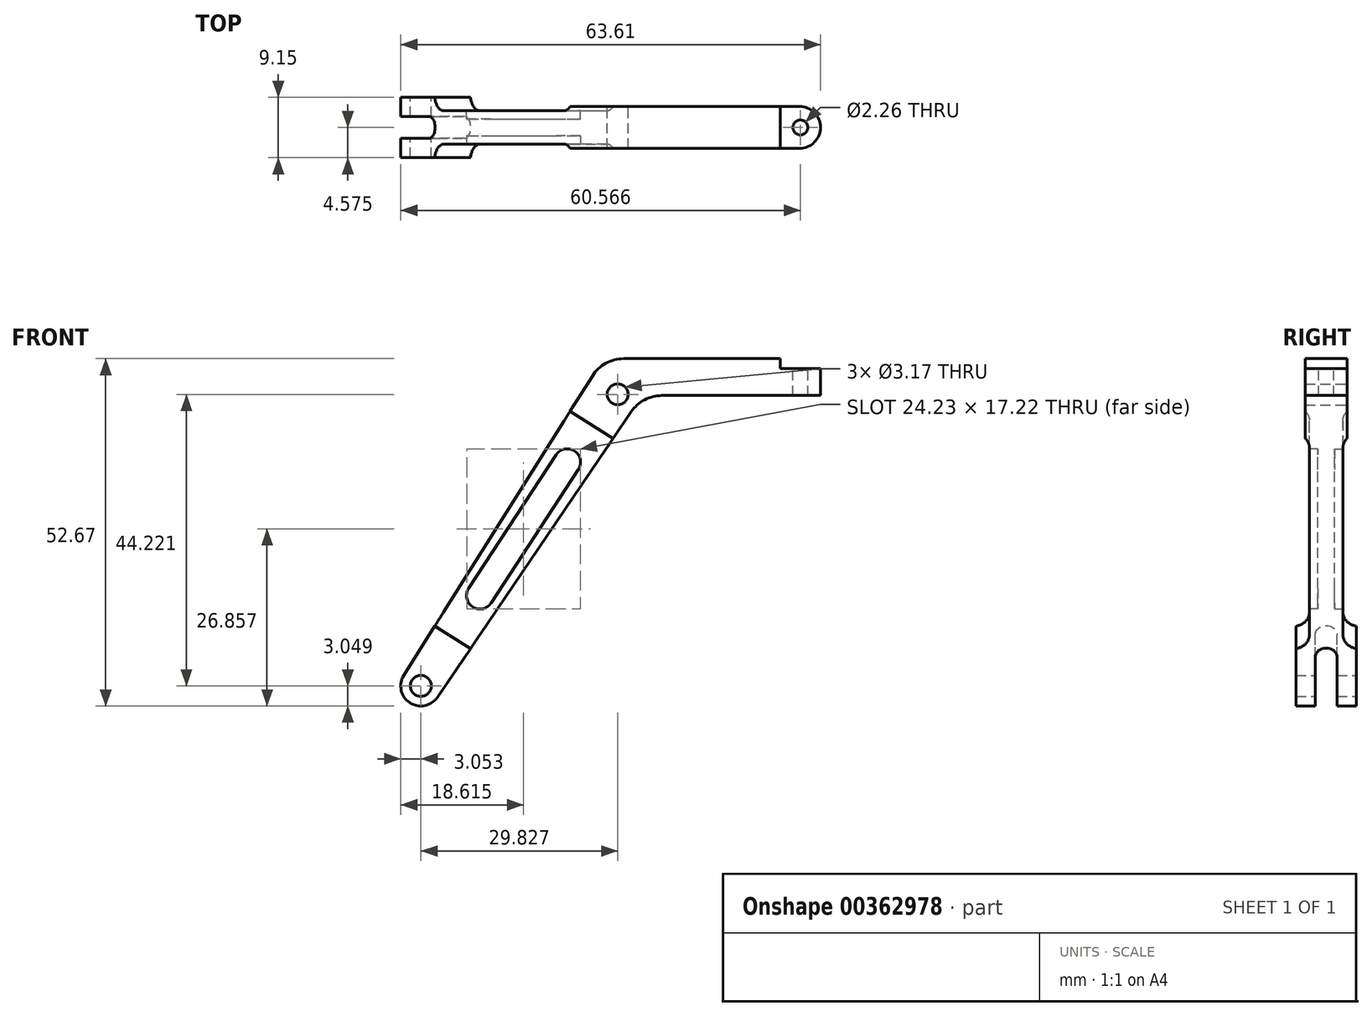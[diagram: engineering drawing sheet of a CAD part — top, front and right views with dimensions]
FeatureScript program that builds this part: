
annotation { "Feature Type Name" : "Feature", "Feature Type Description" : "" }
export const myFeature = defineFeature(function(context is Context, id is Id, definition is map)
    precondition{}
    {
        {
            var Q0;
            Q0=qCreatedBy(makeId("Front.planeOp"),FACE);
            var sketch = newSketch(context, id + "F0", { "sketchPlane" : qUnion([Q0])});
            skCircle(sketch, "E0", {"center": v(0, 0) * mm, "radius": 1.59 * mm});
            skLineSegment(sketch, "E1", {"start": v(30.73, -0.19) * mm, "end": v(30.73, 3.88) * mm});
            skLineSegment(sketch, "E2", {"start": v(0, 0) * mm, "end": v(-29.83, -44.22) * mm, "construction": true});
            skLineSegment(sketch, "E3", {"start": v(0, 0) * mm, "end": v(0, -37.53) * mm, "construction": true});
            skCircle(sketch, "E4", {"center": v(-29.83, -44.22) * mm, "radius": 1.59 * mm});
            skArc(sketch, "E5", {"start": v(-32.4, -42.6) * mm, "mid": v(-31.5, -46.77) * mm, "end": v(-27.3, -45.93) * mm});
            skLineSegment(sketch, "E6", {"start": v(-32.4, -42.6) * mm, "end": v(-3.83, 2.79) * mm});
            skLineSegment(sketch, "E7", {"start": v(0.9, 5.4) * mm, "end": v(24.64, 5.4) * mm});
            skPoint(sketch, "E8.visualSharp", {"position": v(-2.19, 5.4) * mm});
            skArc(sketch, "E8.filletArc", {"start": v(0.9, 5.4) * mm, "mid": v(-1.8, 4.7) * mm, "end": v(-3.83, 2.79) * mm});
            skLineSegment(sketch, "E9", {"start": v(-27.3, -45.93) * mm, "end": v(2.05, -2.64) * mm});
            skLineSegment(sketch, "E10.trimOffspring", {"start": v(6.68, -0.19) * mm, "end": v(30.73, -0.19) * mm});
            skPoint(sketch, "E11.visualSharp", {"position": v(3.72, -0.19) * mm});
            skArc(sketch, "E11.filletArc", {"start": v(6.68, -0.19) * mm, "mid": v(4.06, -0.84) * mm, "end": v(2.05, -2.64) * mm});
            skLineSegment(sketch, "E12", {"start": v(0, 9.08) * mm, "end": v(0, 14.2) * mm});
            skLineSegment(sketch, "E13", {"start": v(24.64, 5.4) * mm, "end": v(24.64, 3.88) * mm});
            skLineSegment(sketch, "E14", {"start": v(24.64, 3.88) * mm, "end": v(30.73, 3.88) * mm});
            skPoint(sketch, "E15.orphan", {"position": v(30.73, 5.4) * mm});
            skPoint(sketch, "E16.0.start.orphan", {"position": v(24.64, 9.08) * mm});
            skSolve(sketch);
        }
        {
            var Q0;
            Q0=makeQuery(id+"F0.imprint","IMPRINT",FACE,{"disambiguationData":[TD([[makeQuery(id+"F0.imprint","IMPRINT",EDGE,{"derivedFrom":sQuery(id+"F0.wireOp",EDGE,"E0")}),-1.0]])]});
            extrude(context, id + "F1", {"entities" : qUnion([Q0]), "depth" : 6.35 * mm});
        }
        {
            var Q0;
            Q0=makeQuery(id+"F1.opExtrude","SWEPT_FACE",FACE,{"disambiguationData":[OSD([sQuery(id+"F0.wireOp",EDGE,"E14")])]});
            var sketch = newSketch(context, id + "F2", { "sketchPlane" : qUnion([Q0])});
            skPoint(sketch, "E17", {"position": v(27.69, -3.18) * mm});
            skPoint(sketch, "E17.positionSnap0", {"position": v(30.73, -3.18) * mm});
            skSolve(sketch);
        }
        {
            var Q0;
            Q0=sQuery(id+"F2.wireOp",VERTEX,"E17");
            var Q1;
            Q1=makeQuery(id+"F1.opExtrude","SWEPT_BODY",BODY,{"disambiguationData":[OSD([sQuery(id+"F0.wireOp",EDGE,"E0"),sQuery(id+"F0.wireOp",EDGE,"E1"),sQuery(id+"F0.wireOp",EDGE,"E4"),sQuery(id+"F0.wireOp",EDGE,"E5"),sQuery(id+"F0.wireOp",EDGE,"E6"),sQuery(id+"F0.wireOp",EDGE,"E7"),sQuery(id+"F0.wireOp",EDGE,"E8.filletArc"),sQuery(id+"F0.wireOp",EDGE,"E9"),sQuery(id+"F0.wireOp",EDGE,"E10.trimOffspring"),sQuery(id+"F0.wireOp",EDGE,"E11.filletArc"),sQuery(id+"F0.wireOp",EDGE,"E13"),sQuery(id+"F0.wireOp",EDGE,"E14")])]});
            hole(context, id + "F3", {"style" : HoleStyle.SIMPLE, "endStyle" : HoleEndStyle.THROUGH, "standardTappedOrClearance" : lookupTablePath({ "standard" : "ANSI", "engagement" : "75%", "pitch" : "40 tpi", "size" : "#4", "type" : "Tapped" }), "standardBlindInLast" : lookupTablePath({ "standard" : "ANSI", "engagement" : "75%", "pitch" : "40 tpi", "size" : "#4", "type" : "Tapped" }), "holeDiameter" : 2.26 * mm, "showTappedDepth" : true, "tappedDepth" : 3 * mm, "tapClearance" : 3, "locations" : qUnion([Q0]), "scope" : qUnion([Q1]), "majorDiameter" : 2.84 * mm});
        }
        {
            var Q0;
            Q0=makeQuery(id+"F1.opExtrude","CAP_EDGE",EDGE,{"disambiguationData":[OSD([sQuery(id+"F0.wireOp",EDGE,"E1")])],"isStart":false});
            var Q1;
            Q1=makeQuery(id+"F1.opExtrude","CAP_EDGE",EDGE,{"disambiguationData":[OSD([sQuery(id+"F0.wireOp",EDGE,"E1")])],"isStart":true});
            fillet(context, id + "F4", {"entities" : qUnion([Q0, Q1]), "radius" : 3.17 * mm, "tangentPropagation" : true, "allowEdgeOverflow" : false});
        }
        {
            var Q0;
            Q0=makeQuery(id+"F1.opExtrude","CAP_FACE",FACE,{"disambiguationData":[OSD([sQuery(id+"F0.wireOp",EDGE,"E0"),sQuery(id+"F0.wireOp",EDGE,"E1"),sQuery(id+"F0.wireOp",EDGE,"E4"),sQuery(id+"F0.wireOp",EDGE,"E5"),sQuery(id+"F0.wireOp",EDGE,"E6"),sQuery(id+"F0.wireOp",EDGE,"E7"),sQuery(id+"F0.wireOp",EDGE,"E8.filletArc"),sQuery(id+"F0.wireOp",EDGE,"E9"),sQuery(id+"F0.wireOp",EDGE,"E10.trimOffspring"),sQuery(id+"F0.wireOp",EDGE,"E11.filletArc"),sQuery(id+"F0.wireOp",EDGE,"E13"),sQuery(id+"F0.wireOp",EDGE,"E14")])],"isStart":false});
            var sketch = newSketch(context, id + "F5", { "sketchPlane" : qUnion([Q0])});
            skLineSegment(sketch, "E18.0", {"start": v(-22.31, -38.57) * mm, "end": v(-27.73, -35.16) * mm});
            skLineSegment(sketch, "E19.0", {"start": v(-32.4, -42.6) * mm, "end": v(-27.73, -35.16) * mm});
            skLineSegment(sketch, "E20.0", {"start": v(-27.3, -45.93) * mm, "end": v(-22.31, -38.57) * mm});
            skArc(sketch, "E21.0", {"start": v(-32.4, -42.6) * mm, "mid": v(-31.5, -46.77) * mm, "end": v(-27.3, -45.93) * mm});
            skPoint(sketch, "E22.orphan", {"position": v(-3.83, 2.79) * mm});
            skPoint(sketch, "E23.orphan", {"position": v(2.05, -2.64) * mm});
            skSolve(sketch);
        }
        {
            var Q0;
            Q0=makeQuery(id+"F5.imprint","IMPRINT",FACE,{"disambiguationData":[TD([[makeQuery(id+"F5.imprint","IMPRINT",EDGE,{"derivedFrom":sQuery(id+"F5.wireOp",EDGE,"E18.0")}),1.0]])]});
            extrude(context, id + "F6", {"entities" : qUnion([Q0]), "operationType" : NewBodyOperationType.ADD, "depth" : 1.4 * mm});
        }
        {
            var Q0;
            Q0=makeQuery(id+"F1.opExtrude","CAP_FACE",FACE,{"disambiguationData":[OSD([sQuery(id+"F0.wireOp",EDGE,"E0"),sQuery(id+"F0.wireOp",EDGE,"E1"),sQuery(id+"F0.wireOp",EDGE,"E4"),sQuery(id+"F0.wireOp",EDGE,"E5"),sQuery(id+"F0.wireOp",EDGE,"E6"),sQuery(id+"F0.wireOp",EDGE,"E7"),sQuery(id+"F0.wireOp",EDGE,"E8.filletArc"),sQuery(id+"F0.wireOp",EDGE,"E9"),sQuery(id+"F0.wireOp",EDGE,"E10.trimOffspring"),sQuery(id+"F0.wireOp",EDGE,"E11.filletArc"),sQuery(id+"F0.wireOp",EDGE,"E13"),sQuery(id+"F0.wireOp",EDGE,"E14")])],"isStart":true});
            var sketch = newSketch(context, id + "F7", { "sketchPlane" : qUnion([Q0])});
            skLineSegment(sketch, "E24.0", {"start": v(32.4, -42.6) * mm, "end": v(3.83, 2.79) * mm});
            skArc(sketch, "E25.0", {"start": v(32.4, -42.6) * mm, "mid": v(31.5, -46.77) * mm, "end": v(27.3, -45.93) * mm});
            skLineSegment(sketch, "E26.0", {"start": v(27.3, -45.93) * mm, "end": v(-2.05, -2.64) * mm});
            skPoint(sketch, "E27.0", {"position": v(22.31, -38.57) * mm});
            skPoint(sketch, "E28.0", {"position": v(27.73, -35.16) * mm});
            skLineSegment(sketch, "E29", {"start": v(22.31, -38.57) * mm, "end": v(27.73, -35.16) * mm});
            skSolve(sketch);
        }
        {
            var Q0;
            {var subQ1=sQuery(id+"F7.wireOp",EDGE,"E25.0");Q0=makeQuery(id+"F7.imprint","IMPRINT",FACE,{"disambiguationData":[TD([[makeQuery(id+"F7.imprint","IMPRINT",EDGE,{"derivedFrom":subQ1}),-1.0]])]});}
            extrude(context, id + "F8", {"entities" : qUnion([Q0]), "operationType" : NewBodyOperationType.ADD, "depth" : 1.4 * mm});
        }
        {
            var Q0;
            Q0=makeQuery(id+"F8.boolean.opBoolean","MERGE",FACE,{"derivedFrom":[makeQuery(id+"F6.boolean.opBoolean","MERGE",FACE,{"derivedFrom":[makeQuery(id+"F1.opExtrude","SWEPT_FACE",FACE,{"disambiguationData":[OSD([sQuery(id+"F0.wireOp",EDGE,"E6")])]}),makeQuery(id+"F6.opExtrude","SWEPT_FACE",FACE,{"disambiguationData":[OSD([sQuery(id+"F5.wireOp",EDGE,"E19.0")])]})]}),makeQuery(id+"F8.opExtrude","SWEPT_FACE",FACE,{"disambiguationData":[OSD([sQuery(id+"F7.wireOp",EDGE,"E24.0")])]})]});
            var sketch = newSketch(context, id + "F9", { "sketchPlane" : qUnion([Q0])});
            skLineSegment(sketch, "E30", {"start": v(7.75, -56.36) * mm, "end": v(-1.4, -56.36) * mm});
            skLineSegment(sketch, "E31.0", {"start": v(-1.4, -53.31) * mm, "end": v(-1.4, -44.53) * mm});
            skLineSegment(sketch, "E32.0", {"start": v(7.75, -53.31) * mm, "end": v(7.75, -44.53) * mm});
            skLineSegment(sketch, "E33.0", {"start": v(1.52, -56.36) * mm, "end": v(1.52, -46.07) * mm});
            skLineSegment(sketch, "E34.0", {"start": v(4.83, -56.36) * mm, "end": v(4.83, -46.07) * mm});
            skArc(sketch, "E35", {"start": v(4.83, -46.07) * mm, "mid": v(3.18, -44.42) * mm, "end": v(1.52, -46.07) * mm});
            skPoint(sketch, "E36.orphan", {"position": v(-1.4, -44.42) * mm});
            skPoint(sketch, "E37.0.start.orphan", {"position": v(7.75, -44.42) * mm});
            skPoint(sketch, "E38.start.orphan", {"position": v(3.18, -44.42) * mm});
            skSolve(sketch);
        }
        {
            var Q0;
            Q0 = qSketchRegion(id + "F9", true);
            extrude(context, id + "F10", {"entities" : qUnion([Q0]), "operationType" : NewBodyOperationType.REMOVE, "endBound" : BoundingType.THROUGH_ALL, "oppositeDirection" : true, "depth" : 25.4 * mm});
        }
        {
            var Q0;
            {var subQ4=sQuery(id+"F9.wireOp",EDGE,"E31.0");Q0=makeQuery(id+"F9.imprint","IMPRINT",FACE,{"disambiguationData":[TD([[makeQuery(id+"F9.imprint","IMPRINT",EDGE,{"derivedFrom":subQ4}),-1.0]])]});}
            var sketch = newSketch(context, id + "F11", { "sketchPlane" : qUnion([Q0])});
            skLineSegment(sketch, "E39.0", {"start": v(6.35, 0.32) * mm, "end": v(0, 0.32) * mm});
            skLineSegment(sketch, "E40.0", {"start": v(6.35, -44.53) * mm, "end": v(6.35, 0.32) * mm});
            skLineSegment(sketch, "E41.0", {"start": v(0, -44.53) * mm, "end": v(0, 0.32) * mm});
            skLineSegment(sketch, "E42.0", {"start": v(5.72, -44.53) * mm, "end": v(5.72, 0.32) * mm});
            skLineSegment(sketch, "E43.0", {"start": v(0.64, -44.53) * mm, "end": v(0.64, 0.32) * mm});
            skPoint(sketch, "E44.orphan", {"position": v(6.35, -1.14) * mm});
            skLineSegment(sketch, "E45", {"start": v(0, -44.53) * mm, "end": v(0.64, -44.53) * mm});
            skLineSegment(sketch, "E46", {"start": v(5.72, -44.53) * mm, "end": v(6.35, -44.53) * mm});
            skLineSegment(sketch, "E47.0", {"start": v(6.35, -6.03) * mm, "end": v(0, -6.03) * mm});
            skSolve(sketch);
        }
        {
            var Q0;
            {var subQ0=sQuery(id+"F11.wireOp",EDGE,"E45");Q0=makeQuery(id+"F11.imprint","IMPRINT",FACE,{"disambiguationData":[TD([[makeQuery(id+"F11.imprint","IMPRINT",EDGE,{"derivedFrom":subQ0}),1.0]])]});}
            var Q1;
            {var subQ0=sQuery(id+"F11.wireOp",EDGE,"E46");Q1=makeQuery(id+"F11.imprint","IMPRINT",FACE,{"disambiguationData":[TD([[makeQuery(id+"F11.imprint","IMPRINT",EDGE,{"derivedFrom":subQ0}),1.0]])]});}
            extrude(context, id + "F12", {"entities" : qUnion([Q0, Q1]), "operationType" : NewBodyOperationType.REMOVE, "endBound" : BoundingType.THROUGH_ALL, "oppositeDirection" : true, "depth" : 25.4 * mm});
        }
        {
            var Q0;
            Q0=makeQuery(id+"F12.boolean.opBoolean","COPY",EDGE,{"derivedFrom":makeQuery(id+"F12.opExtrude","SWEPT_EDGE",EDGE,{"disambiguationData":[OSD([sQuery(id+"F11.wireOp",EDGE,"E42.0"),sQuery(id+"F11.wireOp",EDGE,"E46")])]})});
            var Q1;
            Q1=makeQuery(id+"F12.boolean.opBoolean","COPY",EDGE,{"derivedFrom":makeQuery(id+"F12.opExtrude","SWEPT_EDGE",EDGE,{"disambiguationData":[OSD([sQuery(id+"F11.wireOp",EDGE,"E43.0"),sQuery(id+"F11.wireOp",EDGE,"E45")])]})});
            var Q2;
            Q2=makeQuery(id+"F12.boolean.opBoolean","COPY",EDGE,{"derivedFrom":makeQuery(id+"F12.opExtrude","SWEPT_EDGE",EDGE,{"disambiguationData":[OSD([sQuery(id+"F11.wireOp",EDGE,"E43.0"),sQuery(id+"F11.wireOp",EDGE,"E47.0")])]})});
            var Q3;
            Q3=makeQuery(id+"F12.boolean.opBoolean","COPY",EDGE,{"derivedFrom":makeQuery(id+"F12.opExtrude","SWEPT_EDGE",EDGE,{"disambiguationData":[OSD([sQuery(id+"F11.wireOp",EDGE,"E42.0"),sQuery(id+"F11.wireOp",EDGE,"E47.0")])]})});
            fillet(context, id + "F13", {"entities" : qUnion([Q0, Q1, Q2, Q3]), "radius" : 2.54 * mm, "tangentPropagation" : true, "allowEdgeOverflow" : false});
        }
        {
            var Q0;
            Q0=makeQuery(id+"F12.boolean.opBoolean","COPY",FACE,{"derivedFrom":makeQuery(id+"F12.opExtrude","SWEPT_FACE",FACE,{"disambiguationData":[OSD([sQuery(id+"F11.wireOp",EDGE,"E42.0")])]})});
            var sketch = newSketch(context, id + "F14", { "sketchPlane" : qUnion([Q0])});
            skPoint(sketch, "E48", {"position": v(-4.87, -6.04) * mm});
            skPoint(sketch, "E49", {"position": v(-23.66, -34.78) * mm});
            skLineSegment(sketch, "E50", {"start": v(-23.66, -34.78) * mm, "end": v(-21.99, -32.23) * mm});
            skArc(sketch, "E51", {"start": v(-5.95, -11.4) * mm, "mid": v(-6.54, -8.6) * mm, "end": v(-9.35, -9.18) * mm});
            skArc(sketch, "E52", {"start": v(-22.58, -29.42) * mm, "mid": v(-21.99, -32.23) * mm, "end": v(-19.18, -31.64) * mm});
            skLineSegment(sketch, "E53", {"start": v(-22.58, -29.42) * mm, "end": v(-9.35, -9.18) * mm});
            skLineSegment(sketch, "E54.MirrorCS", {"start": v(-27.06, -32.56) * mm, "end": v(-8.28, -3.82) * mm});
            skLineSegment(sketch, "E55", {"start": v(-19.18, -31.64) * mm, "end": v(-5.95, -11.4) * mm});
            skLineSegment(sketch, "E56.trimOffspring", {"start": v(-6.54, -8.6) * mm, "end": v(-4.87, -6.04) * mm});
            skSolve(sketch);
        }
        {
            var Q0;
            {var subQ3=sQuery(id+"F14.wireOp",EDGE,"E53");Q0=makeQuery(id+"F14.imprint","IMPRINT",FACE,{"disambiguationData":[TD([[makeQuery(id+"F14.imprint","IMPRINT",EDGE,{"derivedFrom":subQ3}),-1.0]])]});}
            extrude(context, id + "F15", {"entities" : qUnion([Q0]), "operationType" : NewBodyOperationType.REMOVE, "oppositeDirection" : true, "depth" : 1.27 * mm});
        }
        {
            var Q0;
            Q0=makeQuery(id+"F12.boolean.opBoolean","COPY",FACE,{"derivedFrom":makeQuery(id+"F12.opExtrude","SWEPT_FACE",FACE,{"disambiguationData":[OSD([sQuery(id+"F11.wireOp",EDGE,"E43.0")])]})});
            var sketch = newSketch(context, id + "F16", { "sketchPlane" : qUnion([Q0])});
            skLineSegment(sketch, "E57.0", {"start": v(22.58, -29.42) * mm, "end": v(9.35, -9.18) * mm});
            skLineSegment(sketch, "E58.0", {"start": v(19.18, -31.64) * mm, "end": v(5.95, -11.4) * mm});
            skArc(sketch, "E59.0", {"start": v(5.95, -11.4) * mm, "mid": v(6.54, -8.6) * mm, "end": v(9.35, -9.18) * mm});
            skArc(sketch, "E60.0", {"start": v(22.58, -29.42) * mm, "mid": v(21.99, -32.23) * mm, "end": v(19.18, -31.64) * mm});
            skSolve(sketch);
        }
        {
            var Q0;
            Q0=makeQuery(id+"F16.imprint","IMPRINT",FACE,{"disambiguationData":[TD([[makeQuery(id+"F16.imprint","IMPRINT",EDGE,{"derivedFrom":sQuery(id+"F16.wireOp",EDGE,"E57.0")}),1.0]])]});
            extrude(context, id + "F17", {"entities" : qUnion([Q0]), "operationType" : NewBodyOperationType.REMOVE, "oppositeDirection" : true, "depth" : 1.27 * mm});
        }
    });
